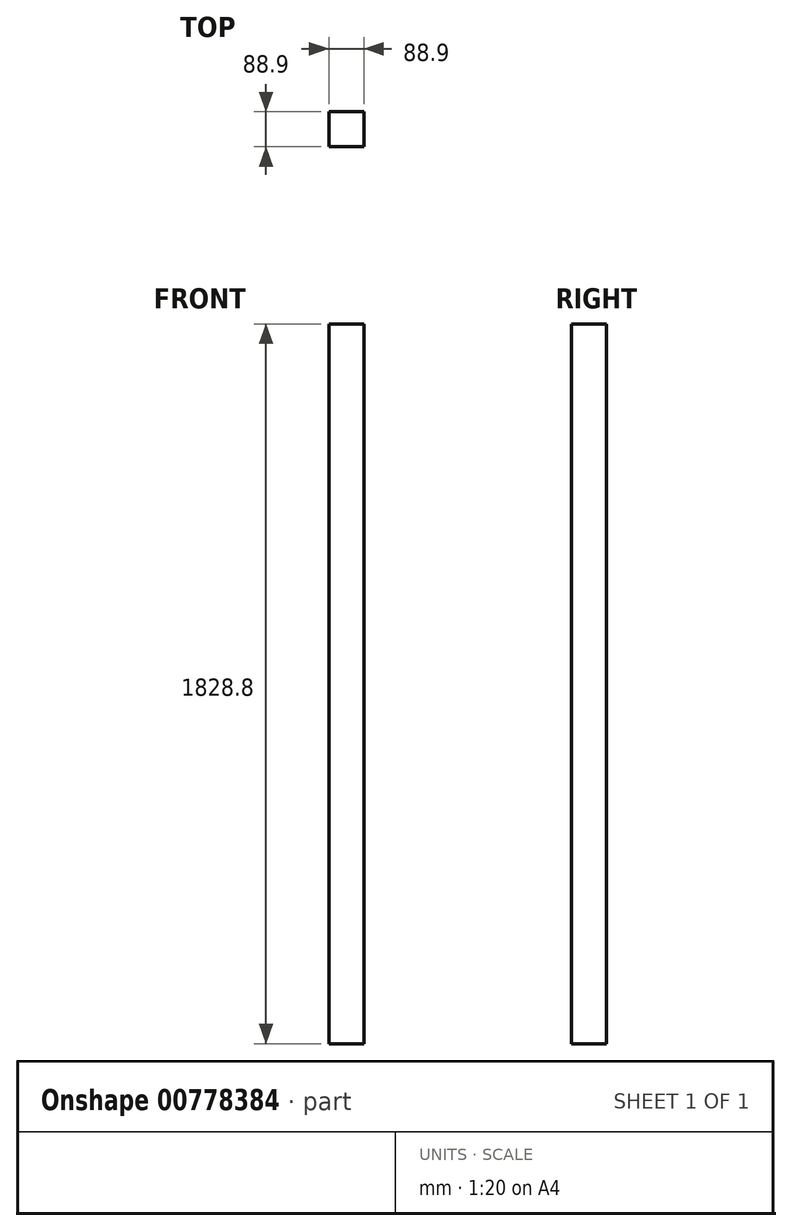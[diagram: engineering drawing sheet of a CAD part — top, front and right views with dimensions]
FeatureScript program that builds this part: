
annotation { "Feature Type Name" : "Feature", "Feature Type Description" : "" }
export const myFeature = defineFeature(function(context is Context, id is Id, definition is map)
    precondition{}
    {
        {
            var Q0;
            Q0=qCreatedBy(makeId("Front.planeOp"),FACE);
            var sketch = newSketch(context, id + "F0", { "sketchPlane" : qUnion([Q0])});
            skLineSegment(sketch, "E0.bottom", {"start": v(0, 0) * mm, "end": v(88.9, 0) * mm});
            skLineSegment(sketch, "E0.top", {"start": v(0, 1828.8) * mm, "end": v(88.9, 1828.8) * mm});
            skLineSegment(sketch, "E0.left", {"start": v(0, 0) * mm, "end": v(0, 1828.8) * mm});
            skLineSegment(sketch, "E0.right", {"start": v(88.9, 0) * mm, "end": v(88.9, 1828.8) * mm});
            skSolve(sketch);
        }
        {
            var Q0;
            Q0 = qSketchRegion(id + "F0", true);
            extrude(context, id + "F1", {"entities" : qUnion([Q0]), "depth" : 88.9 * mm, "offsetDistance" : 25.4 * mm});
        }
    });
